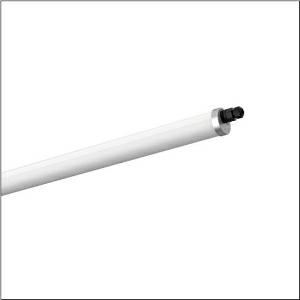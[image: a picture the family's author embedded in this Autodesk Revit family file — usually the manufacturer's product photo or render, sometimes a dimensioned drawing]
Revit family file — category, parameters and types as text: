
# Revit family: monsun_r__31_tube_51ft10dn460a_a449
name_source: partatom
category: Lighting Fixtures
units: mm (PartAtom-declared; Revit-internal decimal feet)

## family parameters
Cut with Voids When Loaded = No
Host = Face
Light Source = No
Part Type = Normal
Room Calculation Point = No
Round Connector Dimension = Use Diameter
Shared = No

## types (1)
- Monsun® 31 Tube (1 x LED, 6500 lm, 40 W, 4000K)
    Apparent Load = 40 VA
    CIE Flux Codes = 42 71 90 91 100
    Color Rendering = 80
    Color Temperature = 4000K
    Default Elevation = 1800 mm
    Description = Monsun® 31 Tube, tubular luminaire, primary optical cover: diffuser, of PMMA, light emission: direct distribution, primary light characteristic: symmetric, installation type: suspended mounting, surface-mounted, LED, rated luminous flux: 6.500lm, luminous efficacy: 160lm/W, light colour: 840, colour temperature: 4000K, with with 1 terminal, 5-pole, max. 2.5mm², through-wiring: 5x 1.5mm², mains connection: 220..240V, AC, 50/60Hz, rated input power: 41W, housing, cylindrical, of PMMA, semi-transparent, matt white, length: 1.570mm, diameter: 75mm, end cap, of stainless steel (V2A), protection rating (complete): IP67/IP69K, insulation class (complete): insulation class I (protective earthing), certification: CE, UKCA, impact resistance: IK07, permissible operating ambient temperature: -20..+40°C, corresponds to IFS (International Featured Standards) requirements for safety and quality in the food industry, packaging unit: 1 piece
    Height = 83 mm
    Lamp = 1 x LED
    Lamp Light Flux = 6500 lm
    Lamp Power = 40 W
    Lamp count = 1
    Length = 1570 mm
    Luminous efficacy = 163 lm/W
    Manufacturer = Siteco
    ModVariant = No
    Model = 51FT10DN460A
    Mounting Place = Ceiling
    Mounting Type = Pendant
    Number of Poles = 1
    OnlyDefault = Yes
    Power Factor = 1
    Product Name = Monsun® 31 Tube
    Product group = tubular luminaire
    ProductGroupID = 907
    Protection Class = Protection class I
    RLX_Detail_Level = 1
    RlxData = <blob elided: 24825 chars, md5=04e060db>
    Socket = socket
    Standby Power = 0 W
    System Light Flux = 6500 lm
    System Power = 40 W
    Type Comments = Product without accessories
    Type Image = l_1228461.jpg
    URL = http://relux.com
    VarID = ---
    Voltage = 0 V
    Weight = 0.00 kg
    Width = 75 mm

## geometry (parser evidence)
native form markers: Blend x4, Sweep x13
no freeform markers — native parametric forms only
